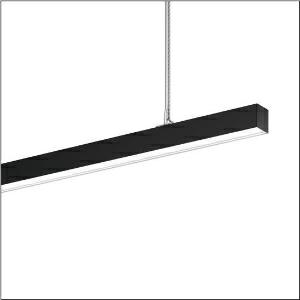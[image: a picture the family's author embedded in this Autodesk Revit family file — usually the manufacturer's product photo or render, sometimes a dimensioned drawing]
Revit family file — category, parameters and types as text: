
# Revit family: silica_r__21_51mx30db35bb_2e66
name_source: partatom
category: Lighting Fixtures
units: mm (PartAtom-declared; Revit-internal decimal feet)

## family parameters
Cut with Voids When Loaded = No
Host = Face
Light Source = No
Part Type = Normal
Room Calculation Point = No
Round Connector Dimension = Use Diameter
Shared = No

## types (1)
- --- (1 x LED, 5260 lm, 34.1 W, 3000K)
    Apparent Load = 34 VA
    CIE Flux Codes = 47 79 96 57 100
    Color Rendering = 80
    Color Temperature = 3000K
    Default Elevation = 1800 mm
    Description = Silica® 21, office luminaire, primary optical cover: cover, of PMMA, opal, light emission: direct/indirect distribution, primary light characteristic: symmetric, installation type: suspended mounting, LED, rated luminous flux: 5.260lm, luminous efficacy: 154lm/W, light colour: 830, colour temperature: 3000K, with terminal, 3+2-pole, max. 2.5mm², mains connection: 220..240V, AC, 50/60Hz, rated input power: 34.1W, luminaire housing, of aluminium, jet black (RAL 9005), length: 1.504mm, width: 53mm, height: 53mm, protection rating (complete): IP20, insulation class (complete): insulation class I (protective earthing), certification: CE, permissible operating ambient temperature: 0..+35°C, standard: EN 50419, packaging unit: 1 piece
    Height = 53 mm
    Lamp = 1 x LED
    Lamp Light Flux = 5260 lm
    Lamp Power = 34.1 W
    Lamp count = 1
    Length = 1504 mm
    Luminous efficacy = 154 lm/W
    Manufacturer = Siteco
    ModVariant = No
    Model = 51MX30DB35BB
    Mounting Place = Ceiling
    Mounting Type = Pendant
    Number of Poles = 1
    OnlyDefault = Yes
    Power Factor = 1
    Product Name = Silica® 21
    Product group = office luminaire | ceiling pendant
    ProductGroupID = 902
    Protection Class = Protection class I
    Protection Degree = IP 20
    RLX_Detail_Level = 1
    RLX_Emergency_Light_Flux = 0 lm
    RLX_Emergency_Type = 0
    RLX_Emergency_Type_DB = No
    RlxData = <blob elided: 26137 chars, md5=53202637>
    Socket = socket
    Standby Power = 0 W
    System Light Flux = 5260 lm
    System Power = 34 W
    Type Comments = factory setting: luminous flux: 100 % | dim-lin: 254 | 233 mA
    Type Image = l_1335856.jpg
    URL = http://relux.com
    VarID = @adj_085825
    Voltage = 0 V
    Weight = 0.00 kg
    Width = 53 mm

## geometry (parser evidence)
native form markers: Blend x4, Sweep x15
no freeform markers — native parametric forms only
